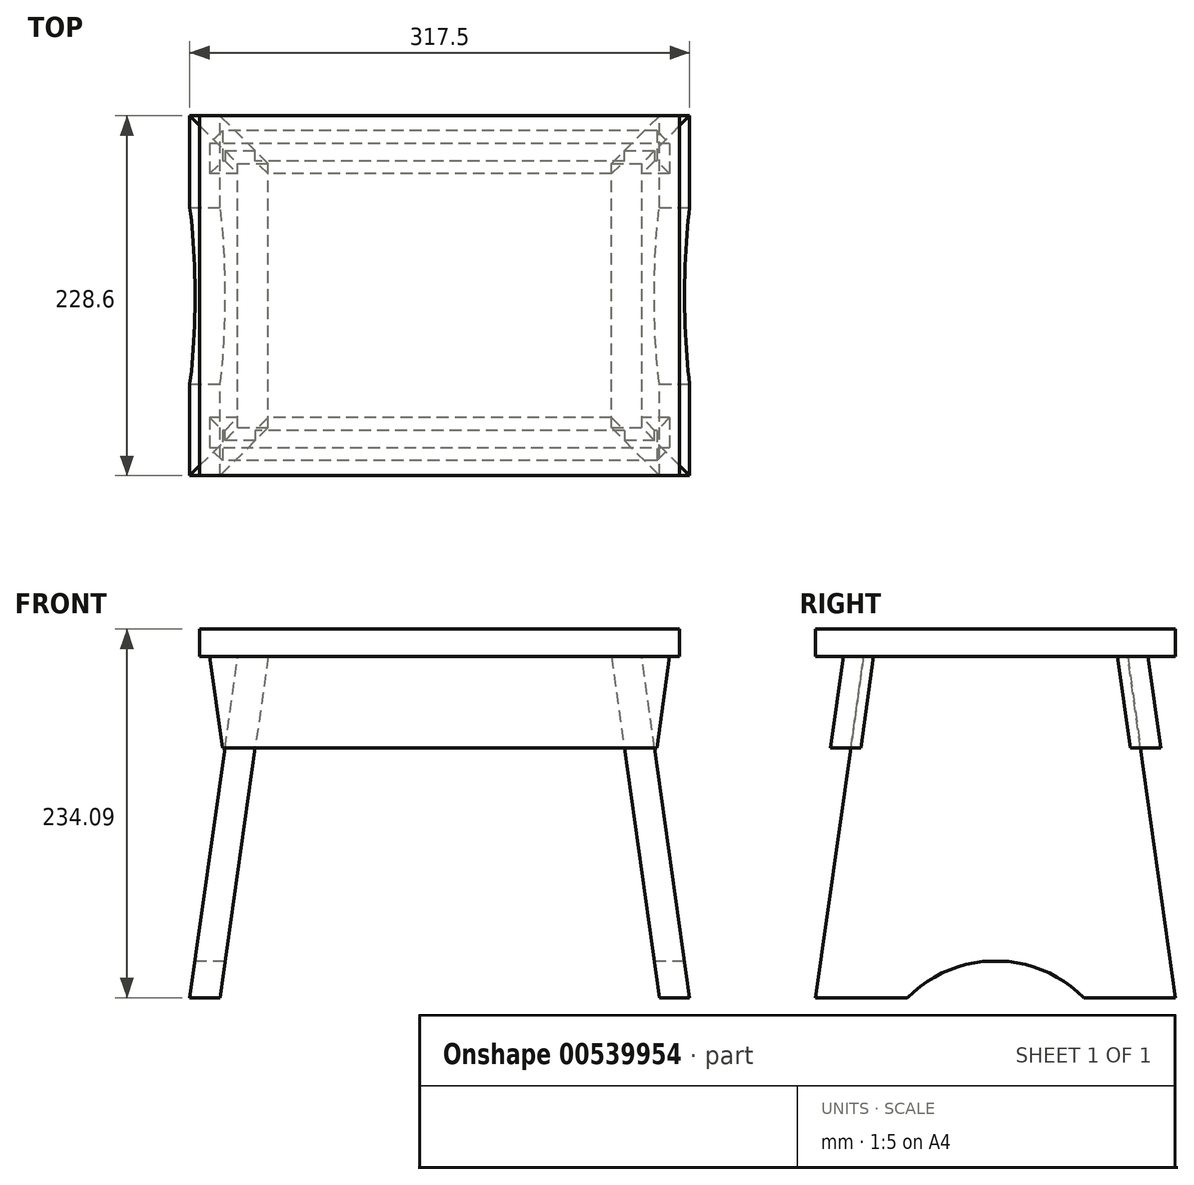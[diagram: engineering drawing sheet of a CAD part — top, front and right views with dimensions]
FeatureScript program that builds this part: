
annotation { "Feature Type Name" : "Feature", "Feature Type Description" : "" }
export const myFeature = defineFeature(function(context is Context, id is Id, definition is map)
    precondition{}
    {
        {
            var Q0;
            Q0=qCreatedBy(makeId("Front.planeOp"),FACE);
            var sketch = newSketch(context, id + "F0", { "sketchPlane" : qUnion([Q0])});
            skLineSegment(sketch, "E0.bottom", {"start": v(-152.4, -8.73) * mm, "end": v(152.4, -8.73) * mm});
            skLineSegment(sketch, "E0.top", {"start": v(-152.4, 8.73) * mm, "end": v(152.4, 8.73) * mm});
            skLineSegment(sketch, "E0.left", {"start": v(-152.4, -8.73) * mm, "end": v(-152.4, 8.73) * mm});
            skLineSegment(sketch, "E0.right", {"start": v(152.4, -8.73) * mm, "end": v(152.4, 8.73) * mm});
            skPoint(sketch, "E0.middle", {"position": v(0, 0) * mm});
            skLineSegment(sketch, "E1.bottom", {"start": v(-152.4, -8.73) * mm, "end": v(152.4, -8.73) * mm, "construction": true});
            skLineSegment(sketch, "E1.top", {"start": v(-152.4, -225.36) * mm, "end": v(152.4, -225.36) * mm, "construction": true});
            skLineSegment(sketch, "E1.left", {"start": v(-152.4, -8.73) * mm, "end": v(-152.4, -225.36) * mm, "construction": true});
            skLineSegment(sketch, "E1.right", {"start": v(152.4, -8.73) * mm, "end": v(152.4, -225.36) * mm, "construction": true});
            skLineSegment(sketch, "E2", {"start": v(128.3, -8.73) * mm, "end": v(158.75, -225.36) * mm});
            skLineSegment(sketch, "E3", {"start": v(158.75, -225.36) * mm, "end": v(139.51, -225.36) * mm});
            skLineSegment(sketch, "E4", {"start": v(139.51, -225.36) * mm, "end": v(109.07, -8.73) * mm});
            skLineSegment(sketch, "E5", {"start": v(109.07, -8.73) * mm, "end": v(128.3, -8.73) * mm});
            skLineSegment(sketch, "E6", {"start": v(0, 0) * mm, "end": v(0, -225.36) * mm, "construction": true});
            skLineSegment(sketch, "E7.MirrorCS", {"start": v(-128.3, -8.73) * mm, "end": v(-158.75, -225.36) * mm});
            skLineSegment(sketch, "E8.MirrorCS", {"start": v(-158.75, -225.36) * mm, "end": v(-139.51, -225.36) * mm});
            skLineSegment(sketch, "E9.MirrorCS", {"start": v(-109.07, -8.73) * mm, "end": v(-128.3, -8.73) * mm});
            skLineSegment(sketch, "E10.MirrorCS", {"start": v(-139.51, -225.36) * mm, "end": v(-109.07, -8.73) * mm});
            skLineSegment(sketch, "E11.top", {"start": v(-152.4, -66.84) * mm, "end": v(152.4, -66.84) * mm});
            skLineSegment(sketch, "E11.left", {"start": v(-152.4, -8.73) * mm, "end": v(-152.4, -66.84) * mm});
            skLineSegment(sketch, "E11.right", {"start": v(152.4, -8.73) * mm, "end": v(152.4, -66.84) * mm});
            skLineSegment(sketch, "E12", {"start": v(146.05, -8.73) * mm, "end": v(137.88, -66.84) * mm});
            skLineSegment(sketch, "E13.MirrorCS", {"start": v(-146.05, -8.73) * mm, "end": v(-137.88, -66.84) * mm});
            skSolve(sketch);
        }
        {
            var Q0;
            Q0=makeQuery(id+"F0.imprint","IMPRINT",FACE,{"disambiguationData":[TD([[makeQuery(id+"F0.imprint","IMPRINT",EDGE,{"derivedFrom":sQuery(id+"F0.wireOp",EDGE,"E0.top")}),-1.0]])]});
            extrude(context, id + "F1", {"entities" : qUnion([Q0]), "endBound" : BoundingType.SYMMETRIC, "depth" : 228.6 * mm, "offsetDistance" : 25.4 * mm});
        }
        {
            var Q0;
            {var subQ0=sQuery(id+"F0.wireOp",EDGE,"E0.bottom");var subQ1=sQuery(id+"F0.wireOp",EDGE,"E7.MirrorCS");var subQ2=makeQuery(id+"F0.imprint","INTERSECT",VERTEX,{"derivedFrom":[subQ1,subQ0]});Q0=makeQuery(id+"F0.imprint","IMPRINT",FACE,{"disambiguationData":[TD([[makeQuery(id+"F0.imprint","IMPRINT",EDGE,{"disambiguationData":[TD([[subQ2,-1.0]])],"derivedFrom":subQ1}),1.0]])]});}
            var Q1;
            {var subQ0=sQuery(id+"F0.wireOp",EDGE,"E8.MirrorCS");Q1=makeQuery(id+"F0.imprint","IMPRINT",FACE,{"disambiguationData":[TD([[makeQuery(id+"F0.imprint","IMPRINT",EDGE,{"derivedFrom":subQ0}),1.0]])]});}
            var Q2;
            {var subQ0=sQuery(id+"F0.wireOp",EDGE,"E0.bottom");var subQ1=sQuery(id+"F0.wireOp",EDGE,"E2");var subQ2=makeQuery(id+"F0.imprint","INTERSECT",VERTEX,{"derivedFrom":[subQ1,subQ0]});Q2=makeQuery(id+"F0.imprint","IMPRINT",FACE,{"disambiguationData":[TD([[makeQuery(id+"F0.imprint","IMPRINT",EDGE,{"disambiguationData":[TD([[subQ2,-1.0]])],"derivedFrom":subQ1}),-1.0]])]});}
            var Q3;
            {var subQ0=sQuery(id+"F0.wireOp",EDGE,"E3");Q3=makeQuery(id+"F0.imprint","IMPRINT",FACE,{"disambiguationData":[TD([[makeQuery(id+"F0.imprint","IMPRINT",EDGE,{"derivedFrom":subQ0}),-1.0]])]});}
            var Q4;
            Q4=makeQuery(id+"F1.opExtrude","CAP_VERTEX",VERTEX,{"disambiguationData":[OSD([sQuery(id+"F0.wireOp",EDGE,"E0.left"),sQuery(id+"F0.wireOp",EDGE,"E0.bottom"),sQuery(id+"F0.wireOp",EDGE,"E11.left")])],"isStart":false});
            var Q5;
            Q5=makeQuery(id+"F1.opExtrude","CAP_VERTEX",VERTEX,{"disambiguationData":[OSD([sQuery(id+"F0.wireOp",EDGE,"E0.left"),sQuery(id+"F0.wireOp",EDGE,"E0.bottom"),sQuery(id+"F0.wireOp",EDGE,"E11.left")])],"isStart":true});
            extrude(context, id + "F2", {"entities" : qUnion([Q0, Q1, Q2, Q3]), "endBound" : BoundingType.UP_TO_VERTEX, "depth" : 25.4 * mm, "endBoundEntityVertex" : qUnion([Q4]), "offsetDistance" : 25.4 * mm, "hasSecondDirection" : true, "secondDirectionBound" : SecondDirectionBoundingType.UP_TO_VERTEX, "secondDirectionOppositeDirection" : true, "secondDirectionDepth" : 25.4 * mm, "secondDirectionBoundEntityVertex" : qUnion([Q5])});
        }
        {
            var Q0;
            Q0=qCreatedBy(makeId("Right.planeOp"),FACE);
            var sketch = newSketch(context, id + "F3", { "sketchPlane" : qUnion([Q0])});
            skLineSegment(sketch, "E14.0.0", {"start": v(114.3, -8.73) * mm, "end": v(-114.3, -8.73) * mm});
            skLineSegment(sketch, "E14.0.1", {"start": v(-114.3, -8.73) * mm, "end": v(-114.3, -225.36) * mm});
            skLineSegment(sketch, "E14.0.2", {"start": v(-114.3, -225.36) * mm, "end": v(114.3, -225.36) * mm});
            skLineSegment(sketch, "E14.0.3", {"start": v(114.3, -225.36) * mm, "end": v(114.3, -8.73) * mm});
            skLineSegment(sketch, "E15", {"start": v(-114.3, -225.36) * mm, "end": v(-83.86, -8.73) * mm});
            skLineSegment(sketch, "E16.MirrorCS", {"start": v(114.3, -225.36) * mm, "end": v(83.86, -8.73) * mm});
            skArc(sketch, "E17", {"start": v(56.01, -225.36) * mm, "mid": v(0, -202) * mm, "end": v(-56.01, -225.36) * mm});
            skSolve(sketch);
        }
        {
            var Q0;
            {var subQ0=sQuery(id+"F3.wireOp",EDGE,"E14.0.1");Q0=makeQuery(id+"F3.imprint","IMPRINT",FACE,{"disambiguationData":[TD([[makeQuery(id+"F3.imprint","IMPRINT",EDGE,{"derivedFrom":subQ0}),1.0]])]});}
            var Q1;
            {var subQ0=sQuery(id+"F3.wireOp",EDGE,"E17");Q1=makeQuery(id+"F3.imprint","IMPRINT",FACE,{"disambiguationData":[TD([[makeQuery(id+"F3.imprint","IMPRINT",EDGE,{"derivedFrom":subQ0}),1.0]])]});}
            var Q2;
            {var subQ0=sQuery(id+"F3.wireOp",EDGE,"E14.0.3");Q2=makeQuery(id+"F3.imprint","IMPRINT",FACE,{"disambiguationData":[TD([[makeQuery(id+"F3.imprint","IMPRINT",EDGE,{"derivedFrom":subQ0}),1.0]])]});}
            extrude(context, id + "F4", {"entities" : qUnion([Q0, Q1, Q2]), "operationType" : NewBodyOperationType.REMOVE, "endBound" : BoundingType.THROUGH_ALL, "oppositeDirection" : true, "depth" : 25.4 * mm, "offsetDistance" : 25.4 * mm, "hasSecondDirection" : true, "secondDirectionBound" : SecondDirectionBoundingType.THROUGH_ALL, "secondDirectionOppositeDirection" : false, "secondDirectionDepth" : 25.4 * mm});
        }
        {
            var Q0;
            Q0=qCreatedBy(makeId("Right.planeOp"),FACE);
            var sketch = newSketch(context, id + "F5", { "sketchPlane" : qUnion([Q0])});
            skLineSegment(sketch, "E18.0", {"start": v(-83.86, -8.73) * mm, "end": v(-114.3, -225.36) * mm});
            skLineSegment(sketch, "E19.0", {"start": v(114.3, 8.73) * mm, "end": v(-114.3, 8.73) * mm});
            skLineSegment(sketch, "E20.0", {"start": v(83.86, -8.73) * mm, "end": v(114.3, -225.36) * mm});
            skLineSegment(sketch, "E21", {"start": v(-96.68, -8.73) * mm, "end": v(-104.85, -66.84) * mm});
            skLineSegment(sketch, "E22", {"start": v(-104.85, -66.84) * mm, "end": v(-85.6, -66.84) * mm});
            skLineSegment(sketch, "E23", {"start": v(-85.6, -66.84) * mm, "end": v(-74.99, 8.73) * mm});
            skLineSegment(sketch, "E24", {"start": v(-74.99, 8.73) * mm, "end": v(-94.23, 8.73) * mm});
            skLineSegment(sketch, "E25.MirrorCS", {"start": v(85.6, -66.84) * mm, "end": v(77.44, -8.73) * mm});
            skLineSegment(sketch, "E26.MirrorCS", {"start": v(96.68, -8.73) * mm, "end": v(104.85, -66.84) * mm});
            skLineSegment(sketch, "E27.MirrorCS", {"start": v(74.99, 8.73) * mm, "end": v(94.23, 8.73) * mm});
            skLineSegment(sketch, "E28.MirrorCS", {"start": v(104.85, -66.84) * mm, "end": v(85.6, -66.84) * mm});
            skLineSegment(sketch, "E29", {"start": v(-85.6, -66.84) * mm, "end": v(16.17, -66.84) * mm, "construction": true});
            skLineSegment(sketch, "E30.0", {"start": v(-114.3, -8.73) * mm, "end": v(114.3, -8.73) * mm});
            skSolve(sketch);
        }
        {
            var Q0;
            {var subQ5=sQuery(id+"F5.wireOp",EDGE,"E23");Q0=makeQuery(id+"F5.imprint","IMPRINT",FACE,{"disambiguationData":[TD([[makeQuery(id+"F5.imprint","IMPRINT",EDGE,{"derivedFrom":subQ5}),1.0]])]});}
            var Q1;
            {var subQ5=sQuery(id+"F5.wireOp",EDGE,"E21");Q1=makeQuery(id+"F5.imprint","IMPRINT",FACE,{"disambiguationData":[TD([[makeQuery(id+"F5.imprint","IMPRINT",EDGE,{"derivedFrom":subQ5}),1.0]])]});}
            var Q2;
            {var subQ5=sQuery(id+"F5.wireOp",EDGE,"E25.MirrorCS");Q2=makeQuery(id+"F5.imprint","IMPRINT",FACE,{"disambiguationData":[TD([[makeQuery(id+"F5.imprint","IMPRINT",EDGE,{"derivedFrom":subQ5}),-1.0]])]});}
            var Q3;
            {var subQ5=sQuery(id+"F5.wireOp",EDGE,"E26.MirrorCS");Q3=makeQuery(id+"F5.imprint","IMPRINT",FACE,{"disambiguationData":[TD([[makeQuery(id+"F5.imprint","IMPRINT",EDGE,{"derivedFrom":subQ5}),-1.0]])]});}
            var Q4;
            Q4=makeQuery(id+"F1.opExtrude","SWEPT_FACE",FACE,{"disambiguationData":[OSD([sQuery(id+"F0.wireOp",EDGE,"E0.right")])]});
            var Q5;
            Q5=makeQuery(id+"F1.opExtrude","SWEPT_FACE",FACE,{"disambiguationData":[OSD([sQuery(id+"F0.wireOp",EDGE,"E0.left")])]});
            extrude(context, id + "F6", {"entities" : qUnion([Q0, Q1, Q2, Q3]), "endBound" : BoundingType.UP_TO_SURFACE, "depth" : 25.4 * mm, "endBoundEntityFace" : qUnion([Q4]), "offsetDistance" : 25.4 * mm, "hasSecondDirection" : true, "secondDirectionBound" : SecondDirectionBoundingType.UP_TO_SURFACE, "secondDirectionOppositeDirection" : true, "secondDirectionDepth" : 25.4 * mm, "secondDirectionBoundEntityFace" : qUnion([Q5])});
        }
        {
            var Q0;
            {var subQ0=sQuery(id+"F0.wireOp",EDGE,"E11.left");Q0=makeQuery(id+"F0.imprint","IMPRINT",FACE,{"disambiguationData":[TD([[makeQuery(id+"F0.imprint","IMPRINT",EDGE,{"derivedFrom":subQ0}),1.0]])]});}
            var Q1;
            {var subQ0=sQuery(id+"F0.wireOp",EDGE,"E11.right");Q1=makeQuery(id+"F0.imprint","IMPRINT",FACE,{"disambiguationData":[TD([[makeQuery(id+"F0.imprint","IMPRINT",EDGE,{"derivedFrom":subQ0}),-1.0]])]});}
            extrude(context, id + "F7", {"entities" : qUnion([Q0, Q1]), "operationType" : NewBodyOperationType.REMOVE, "endBound" : BoundingType.THROUGH_ALL, "oppositeDirection" : true, "depth" : 25.4 * mm, "offsetDistance" : 25.4 * mm, "hasSecondDirection" : true, "secondDirectionBound" : SecondDirectionBoundingType.THROUGH_ALL, "secondDirectionOppositeDirection" : false, "secondDirectionDepth" : 25.4 * mm});
        }
        {
            var Q0;
            Q0=makeQuery(id+"F2.opExtrude","SWEPT_BODY",BODY,{"disambiguationData":[OSD([sQuery(id+"F0.wireOp",EDGE,"E7.MirrorCS"),sQuery(id+"F0.wireOp",EDGE,"E8.MirrorCS"),sQuery(id+"F0.wireOp",EDGE,"E10.MirrorCS"),sQuery(id+"F0.wireOp",EDGE,"E0.bottom")])]});
            var Q1;
            Q1=makeQuery(id+"F7.boolean.opBoolean","SPLIT",BODY,{"disambiguationData":[OD(1.0)],"derivedFrom":makeQuery(id+"F6.opExtrude","SWEPT_BODY",BODY,{"disambiguationData":[OSD([sQuery(id+"F5.wireOp",EDGE,"E25.MirrorCS"),sQuery(id+"F5.wireOp",EDGE,"E26.MirrorCS"),sQuery(id+"F5.wireOp",EDGE,"E27.MirrorCS"),sQuery(id+"F5.wireOp",EDGE,"E28.MirrorCS")])]})});
            booleanBodies(context, id + "F8", {"operationType" : BooleanOperationType.SUBTRACTION, "tools" : qUnion([Q0]), "targets" : qUnion([Q1]), "keepTools" : true});
        }
        {
            var Q0;
            Q0=makeQuery(id+"F2.opExtrude","SWEPT_BODY",BODY,{"disambiguationData":[OSD([sQuery(id+"F0.wireOp",EDGE,"E2"),sQuery(id+"F0.wireOp",EDGE,"E3"),sQuery(id+"F0.wireOp",EDGE,"E4"),sQuery(id+"F0.wireOp",EDGE,"E0.bottom")])]});
            var Q1;
            Q1=makeQuery(id+"F7.boolean.opBoolean","SPLIT",BODY,{"disambiguationData":[OD(1.0)],"derivedFrom":makeQuery(id+"F6.opExtrude","SWEPT_BODY",BODY,{"disambiguationData":[OSD([sQuery(id+"F5.wireOp",EDGE,"E25.MirrorCS"),sQuery(id+"F5.wireOp",EDGE,"E26.MirrorCS"),sQuery(id+"F5.wireOp",EDGE,"E27.MirrorCS"),sQuery(id+"F5.wireOp",EDGE,"E28.MirrorCS")])]})});
            booleanBodies(context, id + "F9", {"operationType" : BooleanOperationType.SUBTRACTION, "tools" : qUnion([Q0]), "targets" : qUnion([Q1]), "keepTools" : true});
        }
        {
            var Q0;
            Q0=makeQuery(id+"F2.opExtrude","SWEPT_BODY",BODY,{"disambiguationData":[OSD([sQuery(id+"F0.wireOp",EDGE,"E7.MirrorCS"),sQuery(id+"F0.wireOp",EDGE,"E8.MirrorCS"),sQuery(id+"F0.wireOp",EDGE,"E10.MirrorCS"),sQuery(id+"F0.wireOp",EDGE,"E0.bottom")])]});
            var Q1;
            Q1=makeQuery(id+"F7.boolean.opBoolean","SPLIT",BODY,{"disambiguationData":[OD(1.0)],"derivedFrom":makeQuery(id+"F6.opExtrude","SWEPT_BODY",BODY,{"disambiguationData":[OSD([sQuery(id+"F5.wireOp",EDGE,"E21"),sQuery(id+"F5.wireOp",EDGE,"E22"),sQuery(id+"F5.wireOp",EDGE,"E23"),sQuery(id+"F5.wireOp",EDGE,"E24")])]})});
            booleanBodies(context, id + "F10", {"operationType" : BooleanOperationType.SUBTRACTION, "tools" : qUnion([Q0]), "targets" : qUnion([Q1]), "keepTools" : true});
        }
        {
            var Q0;
            Q0=makeQuery(id+"F2.opExtrude","SWEPT_BODY",BODY,{"disambiguationData":[OSD([sQuery(id+"F0.wireOp",EDGE,"E2"),sQuery(id+"F0.wireOp",EDGE,"E3"),sQuery(id+"F0.wireOp",EDGE,"E4"),sQuery(id+"F0.wireOp",EDGE,"E0.bottom")])]});
            var Q1;
            Q1=makeQuery(id+"F7.boolean.opBoolean","SPLIT",BODY,{"disambiguationData":[OD(1.0)],"derivedFrom":makeQuery(id+"F6.opExtrude","SWEPT_BODY",BODY,{"disambiguationData":[OSD([sQuery(id+"F5.wireOp",EDGE,"E21"),sQuery(id+"F5.wireOp",EDGE,"E22"),sQuery(id+"F5.wireOp",EDGE,"E23"),sQuery(id+"F5.wireOp",EDGE,"E24")])]})});
            booleanBodies(context, id + "F11", {"operationType" : BooleanOperationType.SUBTRACTION, "tools" : qUnion([Q0]), "targets" : qUnion([Q1]), "keepTools" : true});
        }
    });
